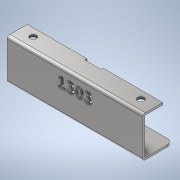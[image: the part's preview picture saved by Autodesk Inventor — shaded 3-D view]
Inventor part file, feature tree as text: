
AUTODESK INVENTOR PART (.ipt)
format: ipt  version: 2020 (Build 240168000, 168)  size: 392,192 bytes
history: native  units: mm
features: other x3, extrude x3, fillet x1, sketch x1, projected_geometry x1
ambient origin geometry x8: Origin, YZ Plane, XZ Plane, XY Plane, X Axis, Y Axis, Z Axis, Center Point
bodies: Body1 (feature_tree)
feature tree (9):
  other  "實體1"
  extrude  "擠出1"  Depth=125.7mm
  extrude  "擠出3"  Depth=26.3mm
  extrude  "擠出4"  Depth=33.0mm
  other  "折彎零件1"
  other  "折彎零件2"
  fillet  "圓角1"  Radius=17.0mm
  sketch  "草圖4"
  projected_geometry  "投影迴路1"
